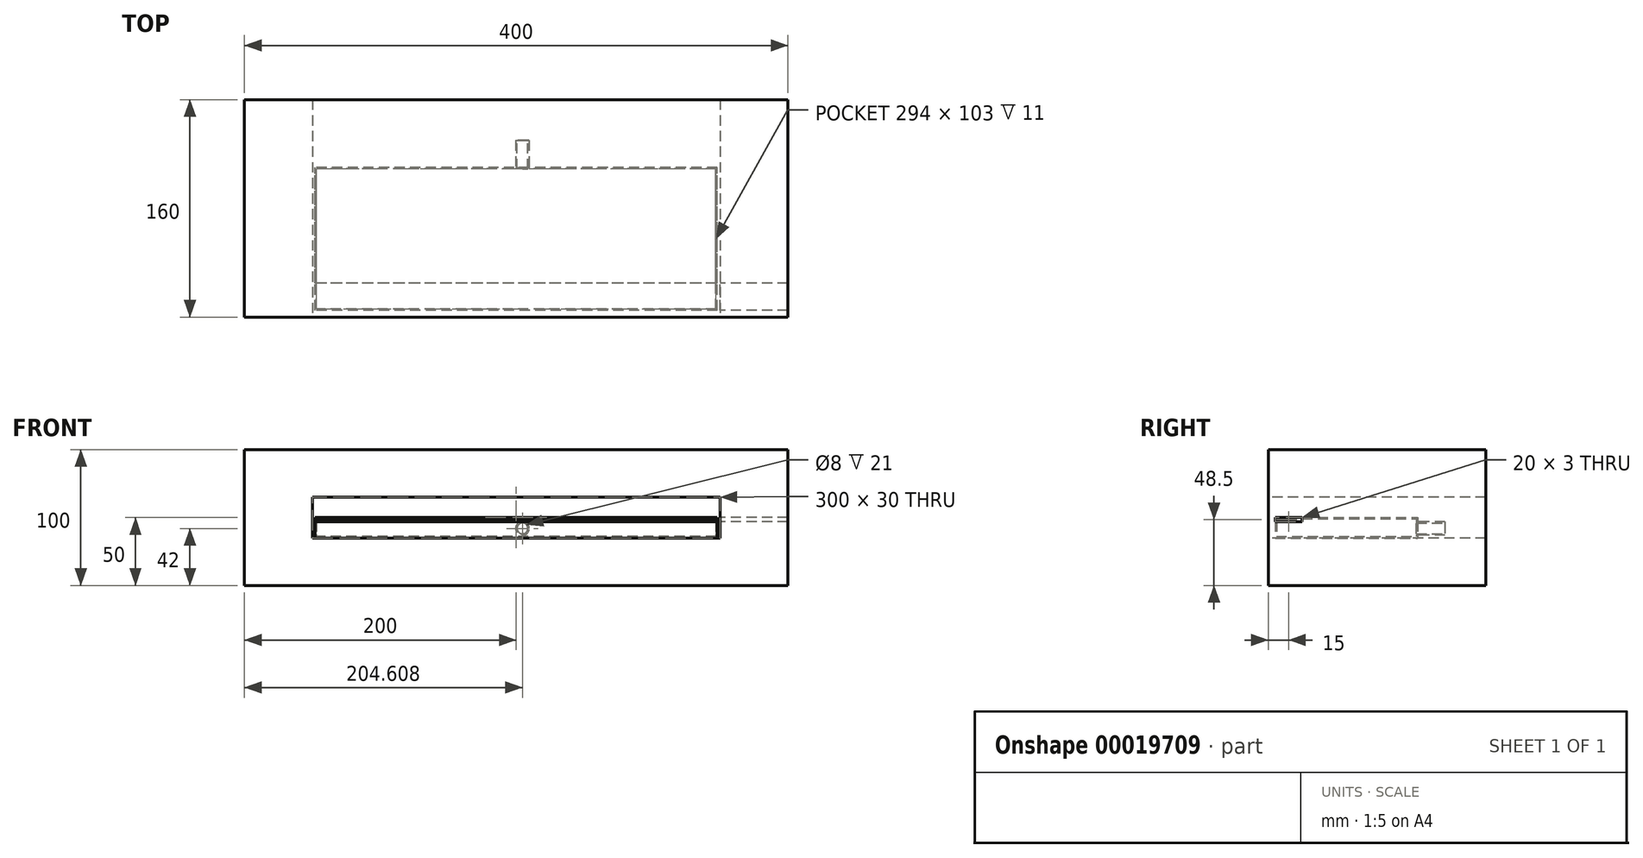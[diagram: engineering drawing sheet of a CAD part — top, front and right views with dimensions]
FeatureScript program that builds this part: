
annotation { "Feature Type Name" : "Feature", "Feature Type Description" : "" }
export const myFeature = defineFeature(function(context is Context, id is Id, definition is map)
    precondition{}
    {
        {
            var Q0;
            Q0=qCreatedBy(makeId("Front.planeOp"),FACE);
            var sketch = newSketch(context, id + "F0", { "sketchPlane" : qUnion([Q0])});
            skLineSegment(sketch, "E0.bottom", {"start": v(0, 0) * mm, "end": v(400, 0) * mm});
            skLineSegment(sketch, "E0.top", {"start": v(0, 100) * mm, "end": v(400, 100) * mm});
            skLineSegment(sketch, "E0.left", {"start": v(0, 0) * mm, "end": v(0, 100) * mm});
            skLineSegment(sketch, "E0.right", {"start": v(400, 0) * mm, "end": v(400, 100) * mm});
            skLineSegment(sketch, "E1", {"start": v(200, 100) * mm, "end": v(200, 0) * mm, "construction": true});
            skLineSegment(sketch, "E2", {"start": v(400, 50) * mm, "end": v(0, 50) * mm, "construction": true});
            skSolve(sketch);
        }
        {
            var Q0;
            Q0=makeQuery(id+"F0.imprint","IMPRINT",FACE,{"disambiguationData":[TD([[makeQuery(id+"F0.imprint","IMPRINT",EDGE,{"derivedFrom":sQuery(id+"F0.wireOp",EDGE,"E0.bottom")}),1.0]])]});
            extrude(context, id + "F1", {"entities" : qUnion([Q0]), "depth" : 160 * mm});
        }
        {
            var Q0;
            Q0=makeQuery(id+"F1.opExtrude","CAP_FACE",FACE,{"disambiguationData":[OSD([sQuery(id+"F0.wireOp",EDGE,"E0.bottom"),sQuery(id+"F0.wireOp",EDGE,"E0.top"),sQuery(id+"F0.wireOp",EDGE,"E0.left"),sQuery(id+"F0.wireOp",EDGE,"E0.right")])],"isStart":false});
            var sketch = newSketch(context, id + "F2", { "sketchPlane" : qUnion([Q0])});
            skLineSegment(sketch, "E3", {"start": v(0, 50) * mm, "end": v(400, 50) * mm, "construction": true});
            skLineSegment(sketch, "E4", {"start": v(200, 100) * mm, "end": v(200, 0) * mm, "construction": true});
            skPoint(sketch, "E5.rect.middle", {"position": v(200, 50) * mm});
            skLineSegment(sketch, "E6.rect.bottom", {"start": v(350, 65) * mm, "end": v(50, 65) * mm});
            skLineSegment(sketch, "E6.rect.top", {"start": v(350, 35) * mm, "end": v(50, 35) * mm});
            skLineSegment(sketch, "E6.rect.left", {"start": v(350, 65) * mm, "end": v(350, 35) * mm});
            skLineSegment(sketch, "E6.rect.right", {"start": v(50, 65) * mm, "end": v(50, 35) * mm});
            skSolve(sketch);
        }
        {
            var Q0;
            Q0 = qSketchRegion(id + "F2", true);
            extrude(context, id + "F3", {"entities" : qUnion([Q0]), "operationType" : NewBodyOperationType.REMOVE, "endBound" : BoundingType.THROUGH_ALL, "oppositeDirection" : true, "depth" : 25 * mm});
        }
        {
            var Q0;
            Q0=makeQuery(id+"F3.boolean.opBoolean","COPY",FACE,{"derivedFrom":makeQuery(id+"F3.opExtrude","SWEPT_FACE",FACE,{"disambiguationData":[OSD([sQuery(id+"F2.wireOp",EDGE,"E6.rect.top")])]})});
            var sketch = newSketch(context, id + "F4", { "sketchPlane" : qUnion([Q0])});
            skLineSegment(sketch, "E7.bottom", {"start": v(348, -155) * mm, "end": v(52, -155) * mm});
            skLineSegment(sketch, "E7.top", {"start": v(348, -50) * mm, "end": v(52, -50) * mm});
            skLineSegment(sketch, "E7.left", {"start": v(348, -155) * mm, "end": v(348, -50) * mm});
            skLineSegment(sketch, "E7.right", {"start": v(52, -155) * mm, "end": v(52, -50) * mm});
            skSolve(sketch);
        }
        {
            var Q0;
            Q0 = qSketchRegion(id + "F4", true);
            extrude(context, id + "F5", {"entities" : qUnion([Q0]), "depth" : 15 * mm});
        }
        {
            var Q0;
            Q0=makeQuery(id+"F5.opExtrude","CAP_FACE",FACE,{"disambiguationData":[OSD([sQuery(id+"F4.wireOp",EDGE,"E7.bottom"),sQuery(id+"F4.wireOp",EDGE,"E7.top"),sQuery(id+"F4.wireOp",EDGE,"E7.left"),sQuery(id+"F4.wireOp",EDGE,"E7.right")])],"isStart":false});
            var Q1;
            Q1=makeQuery(id+"F5.opExtrude","SWEPT_BODY",BODY,{"disambiguationData":[OSD([sQuery(id+"F4.wireOp",EDGE,"E7.bottom"),sQuery(id+"F4.wireOp",EDGE,"E7.top"),sQuery(id+"F4.wireOp",EDGE,"E7.left"),sQuery(id+"F4.wireOp",EDGE,"E7.right")])]});
            shell(context, id + "F6", {"isHollow" : true, "entities" : qUnion([Q0]), "parts" : qUnion([Q1]), "thickness" : 1 * mm});
        }
        {
            var Q0;
            Q0=makeQuery(id+"F5.opExtrude","SWEPT_FACE",FACE,{"disambiguationData":[OSD([sQuery(id+"F4.wireOp",EDGE,"E7.right")])]});
            var sketch = newSketch(context, id + "F7", { "sketchPlane" : qUnion([Q0])});
            skLineSegment(sketch, "E8.bottom", {"start": v(155, 50) * mm, "end": v(135, 50) * mm});
            skLineSegment(sketch, "E8.top", {"start": v(155, 47) * mm, "end": v(135, 47) * mm});
            skLineSegment(sketch, "E8.left", {"start": v(155, 50) * mm, "end": v(155, 47) * mm});
            skLineSegment(sketch, "E8.right", {"start": v(135, 50) * mm, "end": v(135, 47) * mm});
            skSolve(sketch);
        }
        {
            var Q0;
            Q0=makeQuery(id+"F7.imprint","IMPRINT",FACE,{"disambiguationData":[TD([[makeQuery(id+"F7.imprint","IMPRINT",EDGE,{"derivedFrom":sQuery(id+"F7.wireOp",EDGE,"E8.bottom")}),1.0]])]});
            extrude(context, id + "F8", {"entities" : qUnion([Q0]), "operationType" : NewBodyOperationType.REMOVE, "endBound" : BoundingType.THROUGH_ALL, "oppositeDirection" : true, "depth" : 25 * mm});
        }
        {
            var Q0;
            Q0=makeQuery(id+"F5.opExtrude","SWEPT_FACE",FACE,{"disambiguationData":[OSD([sQuery(id+"F4.wireOp",EDGE,"E7.top")])]});
            var sketch = newSketch(context, id + "F9", { "sketchPlane" : qUnion([Q0])});
            skLineSegment(sketch, "E9", {"start": v(-204.6, 50) * mm, "end": v(-204.6, 35) * mm, "construction": true});
            skCircle(sketch, "E10", {"center": v(-204.6, 42) * mm, "radius": 5 * mm});
            skSolve(sketch);
        }
        {
            var Q0;
            Q0 = qSketchRegion(id + "F9", true);
            extrude(context, id + "F10", {"entities" : qUnion([Q0]), "operationType" : NewBodyOperationType.ADD, "depth" : 20 * mm});
        }
        {
            var Q0;
            Q0=makeQuery(id+"F10.opExtrude","CAP_FACE",FACE,{"disambiguationData":[OSD([sQuery(id+"F9.wireOp",EDGE,"E10")])],"isStart":false});
            var sketch = newSketch(context, id + "F11", { "sketchPlane" : qUnion([Q0])});
            skPoint(sketch, "E11", {"position": v(-204.6, 42) * mm});
            skSolve(sketch);
        }
        {
            var Q0;
            Q0=sQuery(id+"F11.wireOp",VERTEX,"E11");
            var Q1;
            Q1=makeQuery(id+"F5.opExtrude","SWEPT_BODY",BODY,{"disambiguationData":[OSD([sQuery(id+"F4.wireOp",EDGE,"E7.bottom"),sQuery(id+"F4.wireOp",EDGE,"E7.top"),sQuery(id+"F4.wireOp",EDGE,"E7.left"),sQuery(id+"F4.wireOp",EDGE,"E7.right")])]});
            hole(context, id + "F12", {"style" : HoleStyle.SIMPLE, "holeDiameter" : 8 * mm, "endStyle" : HoleEndStyle.BLIND, "holeDepth" : 30 * mm, "locations" : qUnion([Q0]), "scope" : qUnion([Q1])});
        }
    });
